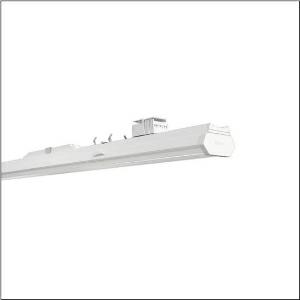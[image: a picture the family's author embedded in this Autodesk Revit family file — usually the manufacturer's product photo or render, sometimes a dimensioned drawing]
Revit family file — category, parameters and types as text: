
# Revit family: licross_r__11_protected_ho_51td12cn4exm_9b5e
name_source: partatom
category: Lighting Fixtures
units: mm (PartAtom-declared; Revit-internal decimal feet)

## family parameters
Cut with Voids When Loaded = No
Host = Face
Light Source = No
Part Type = Normal
Room Calculation Point = No
Round Connector Dimension = Use Diameter
Shared = No

## types (1)
- --- (1 x LED, 14240 lm, 77.6 W, 4000K)
    Apparent Load = 78 VA
    CIE Flux Codes = 70 91 97 98 100
    Color Rendering = 80
    Color Temperature = 4000K
    Default Elevation = 1800 mm
    Description = Licross® 11 Protected HO, luminaire insert, of sheet steel, galvanised, coil coated, white, length: 1.500mm, width: 90mm, height: 101mm, LED rated luminous flux: 14.240lm, light colour: 840, control gear: ON/OFF Multilumen, CLOi, with plug, 3-pole, with phase selection, mains connection: 220..240V, AC, 50/60Hz, halogen-free wiring, primary light control with lens, of plastic, primary optical cover: cover, of PMMA, light emission: direct with ceiling illumination distribution, primary light characteristic: symmetric, protection rating (complete): IP54, insulation class (complete): insulation class I (protective earthing), certification: CE, ENEC, VDE, UKCA, protection symbol: D if used in an environment with non-conductive dust loads with corresponding accessories, impact resistance: IK06, permissible ambient temperature for indoor applications: -35..+35°C, corresponds to IFS (International Featured Standards) requirements for safety and quality in the food industry, reducing of maximum allowable ambient temperature of 5°C with ceiling mounting, LABS conformity tested according to VDMA 24364:2018-05, packaging unit: 1 piece
    Height = 92 mm
    Lamp = 1 x LED
    Lamp Light Flux = 14240 lm
    Lamp Power = 77.6 W
    Lamp count = 1
    Length = 1500 mm
    Luminous efficacy = 184 lm/W
    Manufacturer = Siteco
    ModVariant = No
    Model = 51TD12CN4EXM
    Mounting Place = Ceiling
    Mounting Type = Pendant
    Number of Poles = 1
    OnlyDefault = Yes
    Power Factor = 1
    Product Name = Licross® 11 Protected HO
    Product group = luminaire insert
    ProductGroupID = 902
    Protection Class = Protection class I
    Protection Degree = IP 54
    RLX_Detail_Level = 1
    RlxData = <blob elided: 22149 chars, md5=ac091f62>
    Socket = socket
    Standby Power = 0 W
    System Light Flux = 14240 lm
    System Power = 78 W
    Type Comments = factory setting: luminous flux: 100 % | (A | C | E) | 181 mA
    Type Image = l_1256145.jpg
    URL = http://relux.com
    VarID = @adj_003903
    Voltage = 0 V
    Weight = 0.00 kg
    Width = 88 mm

## geometry (parser evidence)
native form markers: Blend x4, Sweep x9
no freeform markers — native parametric forms only
